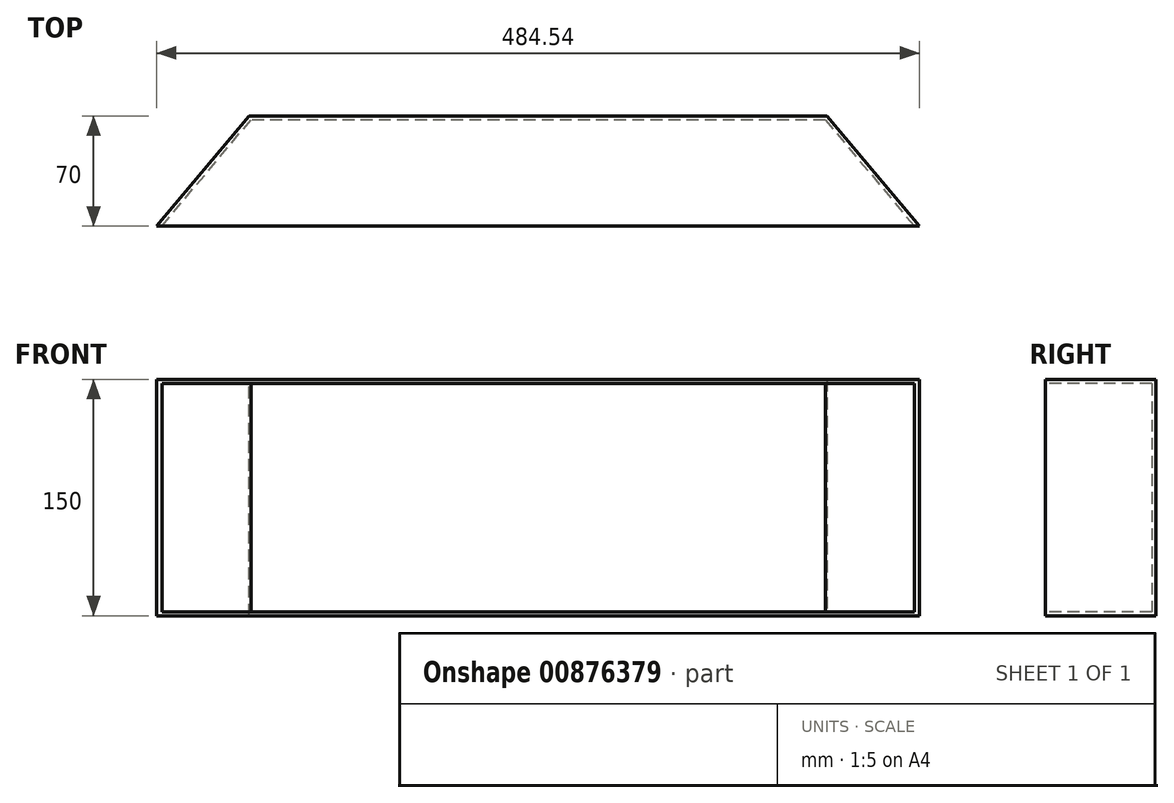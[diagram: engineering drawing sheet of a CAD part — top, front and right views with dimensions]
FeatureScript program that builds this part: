
annotation { "Feature Type Name" : "Feature", "Feature Type Description" : "" }
export const myFeature = defineFeature(function(context is Context, id is Id, definition is map)
    precondition{}
    {
        {
            var Q0;
            Q0=qCreatedBy(makeId("Front.planeOp"),FACE);
            var sketch = newSketch(context, id + "F0", { "sketchPlane" : qUnion([Q0])});
            skLineSegment(sketch, "E0.bottom", {"start": v(183.53, -75) * mm, "end": v(-183.53, -75) * mm});
            skLineSegment(sketch, "E0.top", {"start": v(183.53, 75) * mm, "end": v(-183.53, 75) * mm});
            skLineSegment(sketch, "E0.left", {"start": v(183.53, -75) * mm, "end": v(183.53, 75) * mm});
            skLineSegment(sketch, "E0.right", {"start": v(-183.53, -75) * mm, "end": v(-183.53, 75) * mm});
            skPoint(sketch, "E0.middle", {"position": v(0, 0) * mm});
            skSolve(sketch);
        }
        {
            var Q0;
            Q0 = qSketchRegion(id + "F0", true);
            extrude(context, id + "F1", {"entities" : qUnion([Q0]), "depth" : 70 * mm, "offsetDistance" : 25.4 * mm, "hasDraft" : true, "draftAngle" : 40 * degree});
        }
        {
            var Q0;
            Q0=makeQuery(id+"F1.opExtrude","CAP_FACE",FACE,{"disambiguationData":[OSD([sQuery(id+"F0.wireOp",EDGE,"E0.bottom"),sQuery(id+"F0.wireOp",EDGE,"E0.top"),sQuery(id+"F0.wireOp",EDGE,"E0.left"),sQuery(id+"F0.wireOp",EDGE,"E0.right")])],"isStart":true});
            var sketch = newSketch(context, id + "F2", { "sketchPlane" : qUnion([Q0])});
            skLineSegment(sketch, "E1.bottom", {"start": v(257.06, 75) * mm, "end": v(-302.47, 75) * mm});
            skLineSegment(sketch, "E1.top", {"start": v(257.06, 213.51) * mm, "end": v(-302.47, 213.51) * mm});
            skLineSegment(sketch, "E1.left", {"start": v(257.06, 75) * mm, "end": v(257.06, 213.51) * mm});
            skLineSegment(sketch, "E1.right", {"start": v(-302.47, 75) * mm, "end": v(-302.47, 213.51) * mm});
            skLineSegment(sketch, "E2.bottom", {"start": v(273.3, -75) * mm, "end": v(-315.6, -75) * mm});
            skLineSegment(sketch, "E2.top", {"start": v(273.3, -152.74) * mm, "end": v(-315.6, -152.74) * mm});
            skLineSegment(sketch, "E2.left", {"start": v(273.3, -75) * mm, "end": v(273.3, -152.74) * mm});
            skLineSegment(sketch, "E2.right", {"start": v(-315.6, -75) * mm, "end": v(-315.6, -152.74) * mm});
            skSolve(sketch);
        }
        {
            var Q0;
            Q0=makeQuery(id+"F2.imprint","IMPRINT",FACE,{"disambiguationData":[TD([[makeQuery(id+"F2.imprint","IMPRINT",EDGE,{"derivedFrom":sQuery(id+"F2.wireOp",EDGE,"E2.top")}),-1.0]])]});
            var Q1;
            Q1=makeQuery(id+"F2.imprint","IMPRINT",FACE,{"disambiguationData":[TD([[makeQuery(id+"F2.imprint","IMPRINT",EDGE,{"derivedFrom":sQuery(id+"F2.wireOp",EDGE,"E1.top")}),1.0]])]});
            extrude(context, id + "F3", {"entities" : qUnion([Q0, Q1]), "operationType" : NewBodyOperationType.REMOVE, "oppositeDirection" : true, "depth" : 180.43 * mm, "offsetDistance" : 25.4 * mm});
        }
        {
            var Q0;
            Q0=makeQuery(id+"F1.opExtrude","CAP_FACE",FACE,{"disambiguationData":[OSD([sQuery(id+"F0.wireOp",EDGE,"E0.bottom"),sQuery(id+"F0.wireOp",EDGE,"E0.top"),sQuery(id+"F0.wireOp",EDGE,"E0.left"),sQuery(id+"F0.wireOp",EDGE,"E0.right")])],"isStart":false});
            shell(context, id + "F4", {"entities" : qUnion([Q0]), "thickness" : 2.54 * mm});
        }
    });
